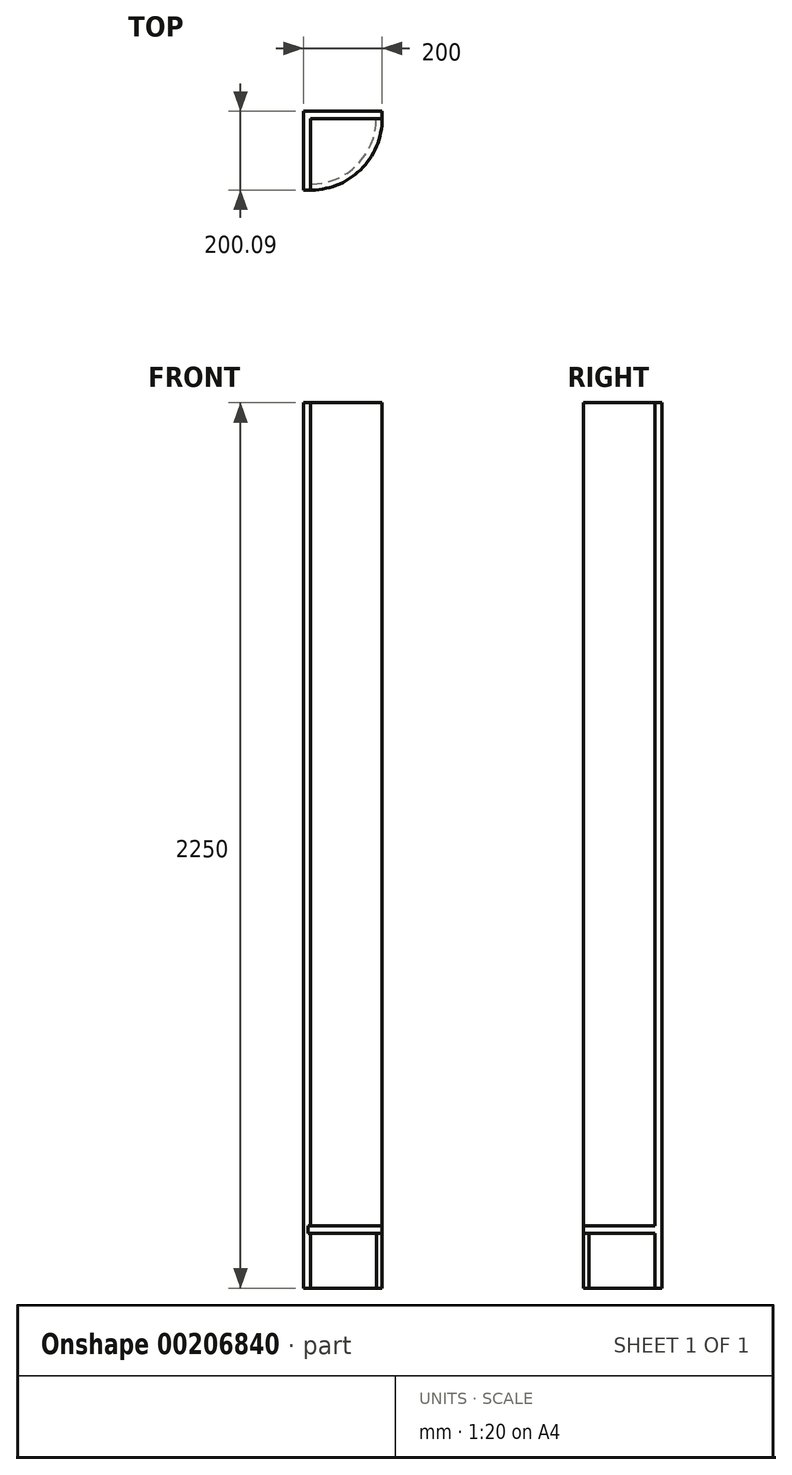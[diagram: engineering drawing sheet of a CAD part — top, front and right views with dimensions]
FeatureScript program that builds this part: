
annotation { "Feature Type Name" : "Feature", "Feature Type Description" : "" }
export const myFeature = defineFeature(function(context is Context, id is Id, definition is map)
    precondition{}
    {
        {
            var Q0;
            Q0=qCreatedBy(makeId("Top.planeOp"),FACE);
            var sketch = newSketch(context, id + "F0", { "sketchPlane" : qUnion([Q0])});
            skLineSegment(sketch, "E0.bottom", {"start": v(-518.83, 154.1) * mm, "end": v(-318.83, 154.1) * mm});
            skLineSegment(sketch, "E0.top", {"start": v(-518.83, -45.9) * mm, "end": v(-500.83, -45.9) * mm});
            skLineSegment(sketch, "E0.left", {"start": v(-518.83, 154.1) * mm, "end": v(-518.83, -45.9) * mm});
            skLineSegment(sketch, "E0.right", {"start": v(-318.83, 154.1) * mm, "end": v(-318.83, 136.1) * mm});
            skLineSegment(sketch, "E1.bottom", {"start": v(-500.83, 136.1) * mm, "end": v(-336.83, 136.1) * mm});
            skLineSegment(sketch, "E1.left", {"start": v(-500.83, 136.1) * mm, "end": v(-500.83, -45.9) * mm});
            skLineSegment(sketch, "E2", {"start": v(-336.83, 136.1) * mm, "end": v(-318.83, 136.1) * mm});
            skSolve(sketch);
        }
        {
            var Q0;
            Q0=qSketchRegion(id+"F0",true);
            extrude(context, id + "F1", {"entities" : qUnion([Q0]), "depth" : 2110 * mm});
        }
        {
            var Q0;
            Q0=qCreatedBy(makeId("Top.planeOp"),FACE);
            var sketch = newSketch(context, id + "F2", { "sketchPlane" : qUnion([Q0])});
            skPoint(sketch, "E3.0", {"position": v(-518.83, 154.1) * mm});
            skLineSegment(sketch, "E4.0", {"start": v(-518.83, 154.1) * mm, "end": v(-518.83, -45.9) * mm});
            skLineSegment(sketch, "E5.0", {"start": v(-518.83, 154.1) * mm, "end": v(-318.83, 154.1) * mm});
            skLineSegment(sketch, "E6.0", {"start": v(-318.83, 154.1) * mm, "end": v(-318.83, 136.1) * mm});
            skLineSegment(sketch, "E7.0", {"start": v(-518.83, -45.9) * mm, "end": v(-500.83, -45.9) * mm});
            skArc(sketch, "E8", {"start": v(-318.83, 136.1) * mm, "mid": v(-374.28, 5.26) * mm, "end": v(-506.85, -45.9) * mm});
            skSolve(sketch);
        }
        {
            var Q0;
            Q0=qSketchRegion(id+"F2",true);
            extrude(context, id + "F3", {"entities" : qUnion([Q0]), "operationType" : NewBodyOperationType.ADD, "depth" : 18 * mm});
        }
        {
            var Q0;
            Q0=qCreatedBy(makeId("Top.planeOp"),FACE);
            var sketch = newSketch(context, id + "F4", { "sketchPlane" : qUnion([Q0])});
            skLineSegment(sketch, "E9.0", {"start": v(-518.83, 154.1) * mm, "end": v(-318.83, 154.1) * mm});
            skLineSegment(sketch, "E10.0", {"start": v(-518.83, 154.1) * mm, "end": v(-518.83, -45.9) * mm});
            skLineSegment(sketch, "E11.0", {"start": v(-518.83, -45.9) * mm, "end": v(-500.83, -45.9) * mm});
            skLineSegment(sketch, "E12.0", {"start": v(-318.83, 154.1) * mm, "end": v(-318.83, 136.1) * mm});
            skLineSegment(sketch, "E13", {"start": v(-500.83, -45.9) * mm, "end": v(-500.83, -30.9) * mm});
            skLineSegment(sketch, "E14", {"start": v(-318.83, 136.1) * mm, "end": v(-333.83, 136.1) * mm});
            skPoint(sketch, "E15.0", {"position": v(-500.83, 136.1) * mm});
            skArc(sketch, "E16", {"start": v(-333.83, 136.1) * mm, "mid": v(-382.75, 18.02) * mm, "end": v(-500.83, -30.9) * mm});
            skSolve(sketch);
        }
        {
            var Q0;
            Q0=qSketchRegion(id+"F4",true);
            extrude(context, id + "F5", {"entities" : qUnion([Q0]), "operationType" : NewBodyOperationType.ADD, "oppositeDirection" : true, "depth" : 140 * mm});
        }
    });
